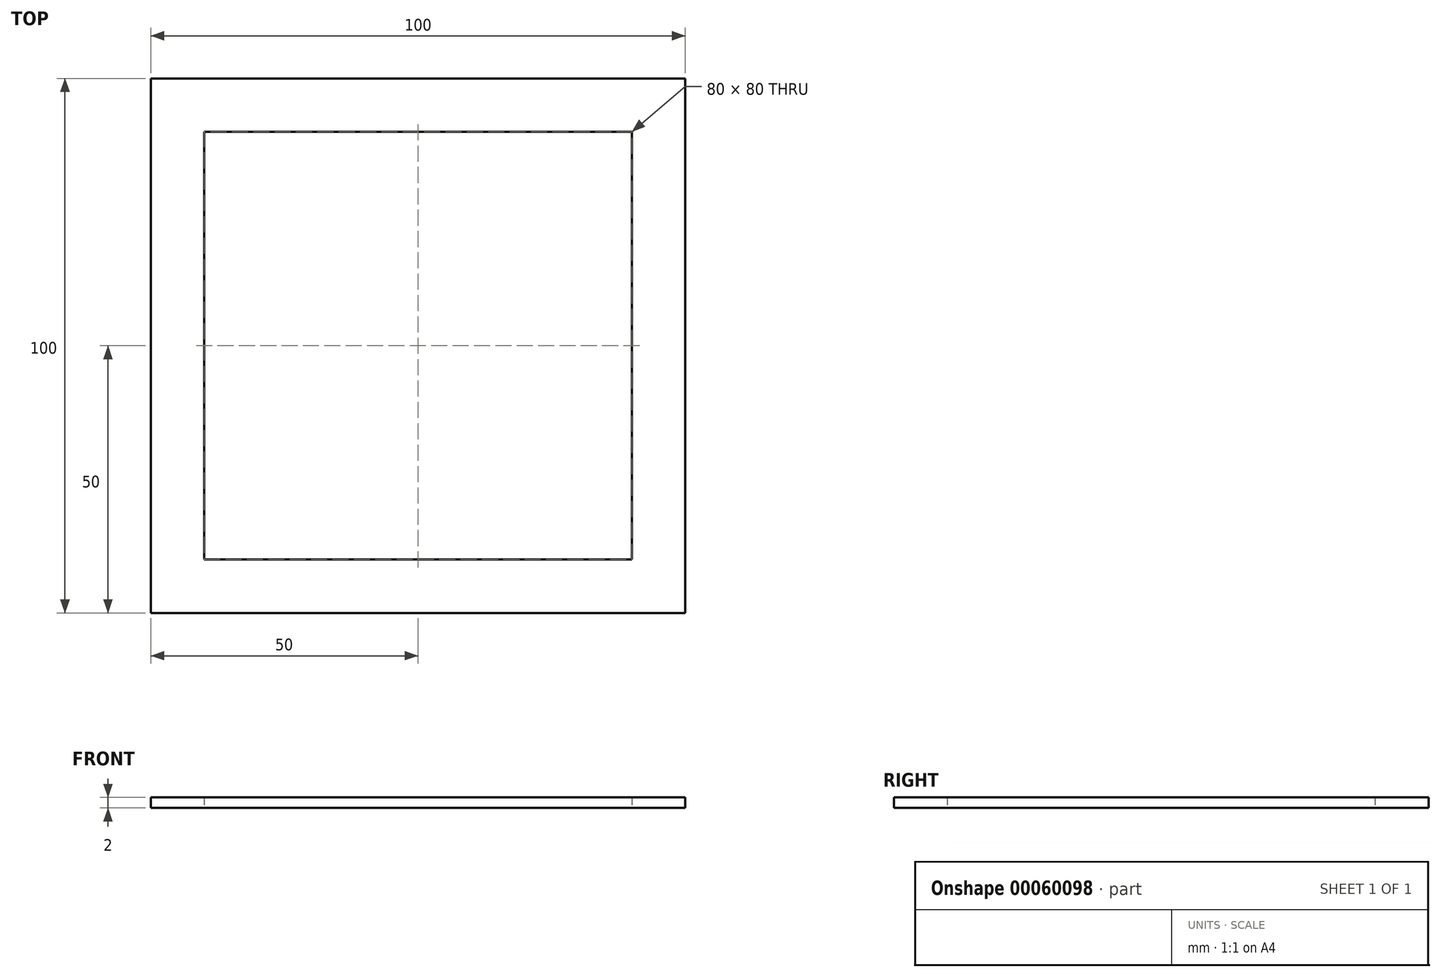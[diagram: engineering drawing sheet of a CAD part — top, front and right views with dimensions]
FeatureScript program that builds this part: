
annotation { "Feature Type Name" : "Feature", "Feature Type Description" : "" }
export const myFeature = defineFeature(function(context is Context, id is Id, definition is map)
    precondition{}
    {
        {
            var Q0;
            Q0=qCreatedBy(makeId("Top.planeOp"),FACE);
            var sketch = newSketch(context, id + "F0", { "sketchPlane" : qUnion([Q0])});
            skLineSegment(sketch, "E0.bottom", {"start": v(0, 0) * mm, "end": v(100, 0) * mm});
            skLineSegment(sketch, "E0.top", {"start": v(0, 100) * mm, "end": v(100, 100) * mm});
            skLineSegment(sketch, "E0.left", {"start": v(0, 0) * mm, "end": v(0, 100) * mm});
            skLineSegment(sketch, "E0.right", {"start": v(100, 0) * mm, "end": v(100, 100) * mm});
            skLineSegment(sketch, "E1.0", {"start": v(10, 10) * mm, "end": v(10, 90) * mm});
            skLineSegment(sketch, "E1.1", {"start": v(10, 10) * mm, "end": v(90, 10) * mm});
            skLineSegment(sketch, "E1.2", {"start": v(90, 10) * mm, "end": v(90, 90) * mm});
            skLineSegment(sketch, "E1.3", {"start": v(10, 90) * mm, "end": v(90, 90) * mm});
            skSolve(sketch);
        }
        {
            var Q0;
            Q0=makeQuery(id+"F0.imprint","IMPRINT",FACE,{"disambiguationData":[TD([[makeQuery(id+"F0.imprint","IMPRINT",EDGE,{"derivedFrom":sQuery(id+"F0.wireOp",EDGE,"E0.bottom")}),1.0]])]});
            extrude(context, id + "F1", {"entities" : qUnion([Q0]), "depth" : 2 * mm});
        }
    });
